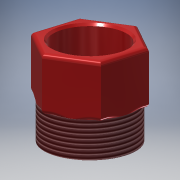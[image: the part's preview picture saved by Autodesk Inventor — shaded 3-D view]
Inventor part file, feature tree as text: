
AUTODESK INVENTOR PART (.ipt)
format: ipt  version: 2018 (Build 220112000, 112)  size: 222,720 bytes
history: native  units: mm
features: extrude x3, sketch x3, fillet x2, chamfer x1, thread x1
ambient origin geometry x8: Origin, YZ Plane, XZ Plane, XY Plane, X Axis, Y Axis, Z Axis, Center Point
bodies: Solid1 (feature_tree)
feature tree (10):
  extrude  "Extrusion1"  Depth=10.0mm TaperAngle=0.0deg
  extrude  "Extrusion2"  Depth=10.0mm
  extrude  "Extrusion3"  Depth=0.5mm TaperAngle=45.0deg
  chamfer  "Chamfer1"  Distance=0.5mm
  fillet  "Fillet1"  Radius=0.5mm
  fillet  "Fillet2"  Radius=4.0mm
  thread  "Thread1"  [1 undecoded]
  sketch  "Sketch1"  dims[d0=10.0mm d1=6.0mm d2=0.0mm]
  sketch  "Sketch2"  dims[d3=10.0mm d4=0.0mm d5=8.0mm]
  sketch  "Sketch3"  dims[d6=6.0mm d7=0.0mm d8=0.25mm d9=2.0mm d10=45.0deg d11=0.5mm d12=0.5mm d13=4.0mm d14=0.0mm]
note: 1 required parameter value undecoded (feature->parameter linkage not recoverable at this tier; creation-order binding heuristic only, values carry confidence <= 0.55)
